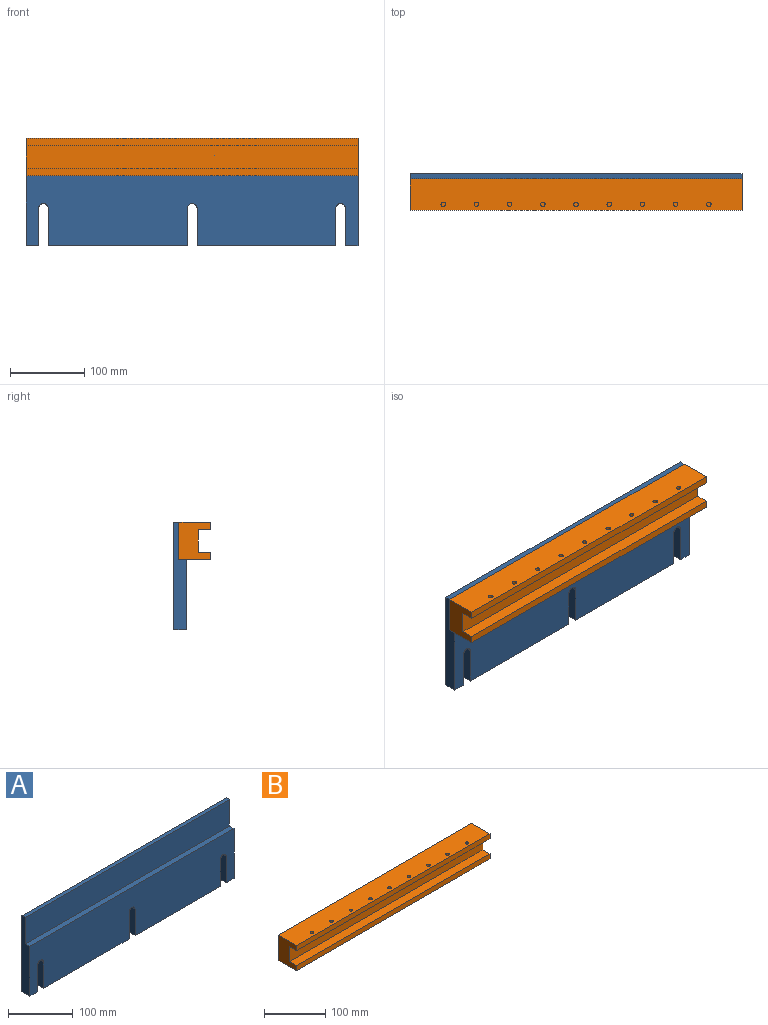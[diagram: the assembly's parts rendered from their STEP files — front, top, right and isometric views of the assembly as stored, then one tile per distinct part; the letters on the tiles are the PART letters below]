
ASSEMBLY  parts=2 mates=1
PART A: 20 faces, bbox 446x17x144 mm
  f0: plane 17x16.8mm, normal (0,0,-1), area 285.6mm2, adj f1,f9,f11,f17
  f1: plane 446x144mm, normal (0,1,0), area 62074.9mm2, adj f0,f2,f3,f4,f5,f6,f7,f8
  f2: plane 186.4x17mm, normal (0,0,-1), area 3168.8mm2, adj f1,f4,f11,f19
  f3: plane 50x17mm, normal (1,0,0), area 850mm2, adj f1,f5,f6,f11
  f4: plane 50x17mm, normal (-1,0,0), area 850mm2, adj f1,f2,f5,f11
  f5: cylinder r=6.5mm len=17mm, axis (0,-1,0), area 347.1mm2, adj f1,f3,f4,f11
  f6: plane 187x17mm, normal (0,0,-1), area 3179mm2, adj f1,f3,f11,f15
  f7: plane 144x17mm, normal (-1,0,0), area 1948mm2, adj f1,f8,f10,f11,f12,f13
  f8: plane 17x16.8mm, normal (0,0,-1), area 285.6mm2, adj f1,f7,f11,f14
  f9: plane 144x17mm, normal (1,0,0), area 1948mm2, adj f0,f1,f10,f11,f12,f13
  f10: plane 446x10mm, normal (0,0,1), area 4460mm2, adj f7,f9,f11,f12
  f11: plane 446x94mm, normal (0,-1,0), area 39774.9mm2, adj f0,f2,f3,f4,f5,f6,f7,f8
  f12: plane 446x50mm, normal (0,-1,0), area 22300mm2, adj f7,f9,f10,f13
  f13: plane 446x7mm, normal (0,0,1), area 3122mm2, adj f1,f7,f9,f12
  f14: plane 50x17mm, normal (1,0,0), area 850mm2, adj f1,f8,f11,f16
  f15: plane 50x17mm, normal (-1,0,0), area 850mm2, adj f1,f6,f11,f16
  f16: cylinder r=6.5mm len=17mm, axis (0,-1,0), area 347.1mm2, adj f1,f11,f14,f15
  f17: plane 50x17mm, normal (-1,0,0), area 850mm2, adj f0,f1,f11,f18
  f18: cylinder r=6.5mm len=17mm, axis (0,-1,0), area 347.1mm2, adj f1,f11,f17,f19
  f19: plane 50x17mm, normal (1,0,0), area 850mm2, adj f1,f2,f11,f18
PART B: 19 faces, bbox 446x42x50 mm
  f0: cylinder r=3mm len=10mm, axis (0,0,1), area 188.5mm2, adj f12,f15
  f1: cylinder r=3mm len=10mm, axis (0,0,1), area 188.5mm2, adj f12,f15
  f2: cylinder r=3mm len=10mm, axis (0,0,1), area 188.5mm2, adj f12,f15
  f3: cylinder r=3mm len=10mm, axis (0,0,1), area 188.5mm2, adj f12,f15
  f4: cylinder r=3mm len=10mm, axis (0,0,1), area 188.5mm2, adj f12,f15
  f5: cylinder r=3mm len=10mm, axis (0,0,1), area 188.5mm2, adj f12,f15
  f6: cylinder r=3mm len=10mm, axis (0,0,1), area 188.5mm2, adj f12,f15
  f7: cylinder r=3mm len=10mm, axis (0,0,1), area 188.5mm2, adj f12,f15
  f8: plane 446x10mm, normal (0,-1,0), area 4460mm2, adj f9,f10,f11,f17
  f9: plane 50x42mm, normal (1,0,0), area 1614mm2, adj f8,f11,f12,f13,f14,f15,f16,f17
  f10: plane 50x42mm, normal (-1,0,0), area 1614mm2, adj f8,f11,f12,f13,f14,f15,f16,f17
  f11: plane 446x42mm, normal (0,0,-1), area 18732mm2, adj f8,f9,f10,f14
  f12: plane 446x42mm, normal (0,0,1), area 18477.5mm2, adj f0,f1,f2,f3,f4,f5,f6,f7
  f13: plane 446x10mm, normal (0,-1,0), area 4460mm2, adj f9,f10,f12,f15
  f14: plane 446x50mm, normal (0,1,0), area 22300mm2, adj f9,f10,f11,f12
  f15: plane 446x16.2mm, normal (0,0,-1), area 6970.7mm2, adj f0,f1,f2,f3,f4,f5,f6,f7
  f16: plane 446x30mm, normal (0,-1,0), area 13380mm2, adj f9,f10,f15,f17
  f17: plane 446x16.2mm, normal (0,0,1), area 7225.2mm2, adj f8,f9,f10,f16
  f18: cylinder r=3mm len=10mm, axis (0,0,1), area 188.5mm2, adj f12,f15
PLACE A t=(-222.04,8.8,-72.39)mm
PLACE B t=(-222.04,1.8,21.61)mm
MATE fastened B.f14 <-> A.f12  axis (0,1,0) through (0.96,1.8,46.61)mm
